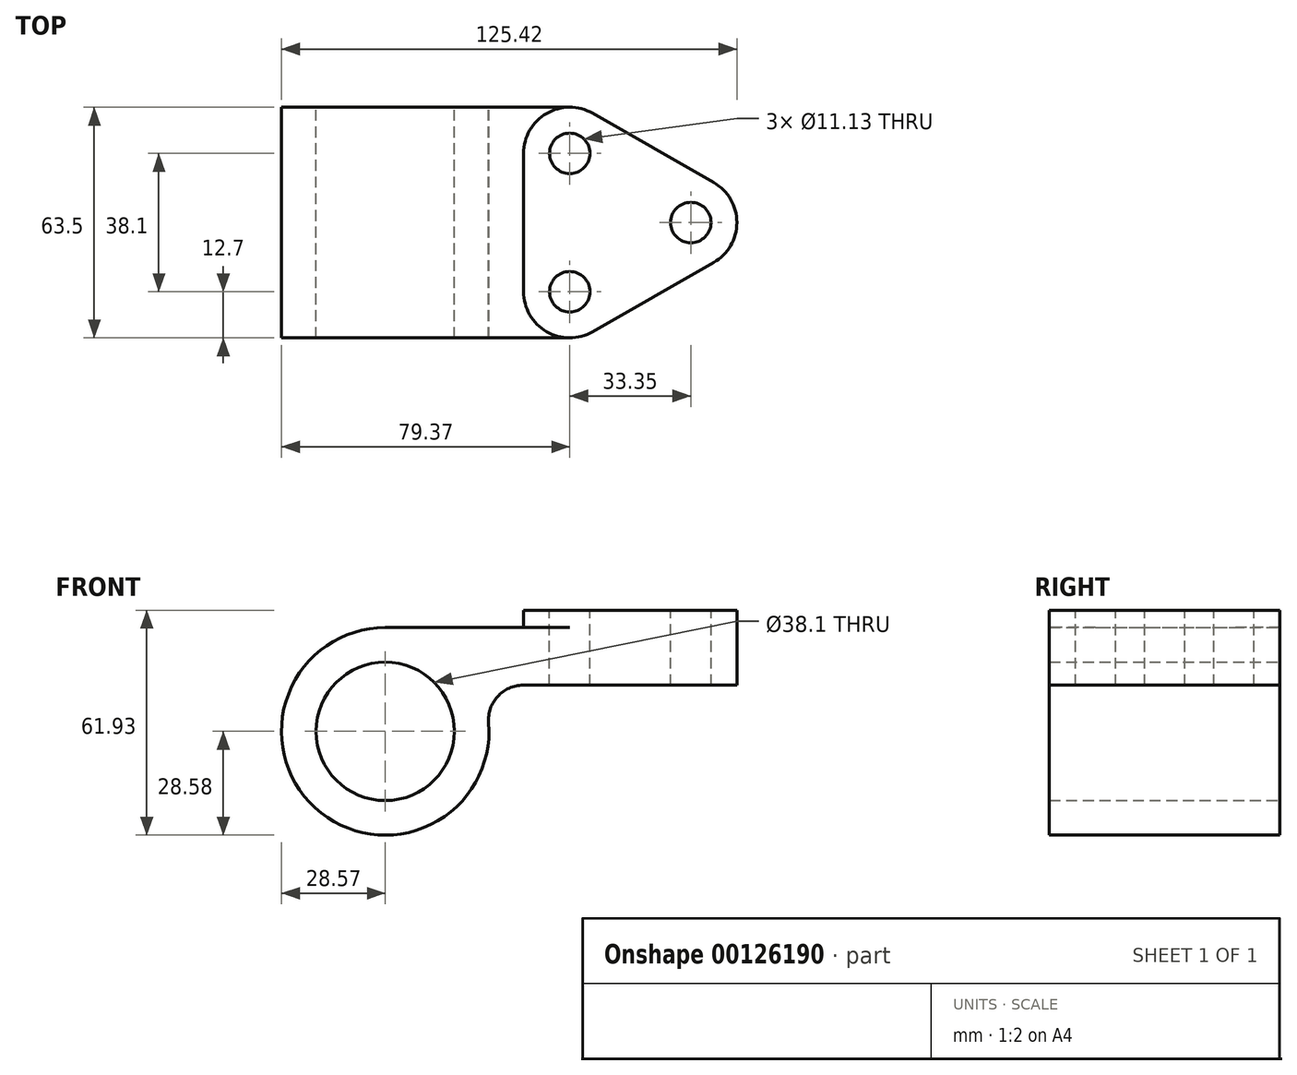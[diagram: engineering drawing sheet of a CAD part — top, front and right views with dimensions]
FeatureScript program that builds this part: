
annotation { "Feature Type Name" : "Feature", "Feature Type Description" : "" }
export const myFeature = defineFeature(function(context is Context, id is Id, definition is map)
    precondition{}
    {
        {
            var Q0;
            Q0=qCreatedBy(makeId("Front.planeOp"),FACE);
            var sketch = newSketch(context, id + "F0", { "sketchPlane" : qUnion([Q0])});
            skArc(sketch, "E0", {"start": v(0, 28.58) * mm, "mid": v(-19.35, -21.03) * mm, "end": v(28.48, 2.38) * mm});
            skArc(sketch, "E1", {"start": v(37.97, 12.7) * mm, "mid": v(30.96, 9.62) * mm, "end": v(28.48, 2.38) * mm});
            skLineSegment(sketch, "E2", {"start": v(0, 28.58) * mm, "end": v(38.1, 28.58) * mm});
            skCircle(sketch, "E3", {"center": v(0, 0) * mm, "radius": 19.05 * mm});
            skLineSegment(sketch, "E4", {"start": v(38.1, 28.58) * mm, "end": v(38.1, 33.35) * mm});
            skLineSegment(sketch, "E5", {"start": v(38.1, 33.35) * mm, "end": v(96.85, 33.35) * mm});
            skLineSegment(sketch, "E6", {"start": v(96.85, 33.35) * mm, "end": v(96.85, 12.7) * mm});
            skLineSegment(sketch, "E7", {"start": v(37.97, 12.7) * mm, "end": v(96.85, 12.7) * mm});
            skLineSegment(sketch, "E8", {"start": v(19.74, -20.66) * mm, "end": v(69.85, 12.7) * mm, "construction": true});
            skLineSegment(sketch, "E9", {"start": v(84.15, 12.7) * mm, "end": v(84.15, 33.35) * mm, "construction": true});
            skLineSegment(sketch, "E10", {"start": v(50.8, 12.7) * mm, "end": v(50.8, 33.35) * mm, "construction": true});
            skSolve(sketch);
        }
        {
            var Q0;
            Q0 = qSketchRegion(id + "F0", true);
            extrude(context, id + "F1", {"entities" : qUnion([Q0]), "depth" : 63.5 * mm});
        }
        {
            var Q0;
            Q0=makeQuery(id+"F1.opExtrude","SWEPT_FACE",FACE,{"disambiguationData":[OSD([sQuery(id+"F0.wireOp",EDGE,"E5")])]});
            var sketch = newSketch(context, id + "F2", { "sketchPlane" : qUnion([Q0])});
            skCircle(sketch, "E11", {"center": v(50.8, -12.7) * mm, "radius": 5.56 * mm});
            skCircle(sketch, "E12", {"center": v(50.8, -50.8) * mm, "radius": 5.56 * mm});
            skCircle(sketch, "E13", {"center": v(84.15, -31.75) * mm, "radius": 5.56 * mm});
            skLineSegment(sketch, "E14", {"start": v(96.85, -31.75) * mm, "end": v(-50.82, -31.75) * mm, "construction": true});
            skPoint(sketch, "E14.endSnap0", {"position": v(96.85, -31.75) * mm});
            skLineSegment(sketch, "E15", {"start": v(84.15, -87.19) * mm, "end": v(84.15, 6.07) * mm, "construction": true});
            skLineSegment(sketch, "E16", {"start": v(33.35, -98.65) * mm, "end": v(33.35, 81.53) * mm, "construction": true});
            skLineSegment(sketch, "E17", {"start": v(50.8, 11.94) * mm, "end": v(50.8, -91.8) * mm, "construction": true});
            skArc(sketch, "E18", {"start": v(90.45, -42.78) * mm, "mid": v(96.85, -31.75) * mm, "end": v(90.45, -20.72) * mm});
            skArc(sketch, "E19", {"start": v(57.1, -1.67) * mm, "mid": v(44.42, -1.72) * mm, "end": v(38.1, -12.7) * mm});
            skArc(sketch, "E20", {"start": v(38.1, -50.8) * mm, "mid": v(44.42, -61.78) * mm, "end": v(57.1, -61.83) * mm});
            skLineSegment(sketch, "E21", {"start": v(57.1, -1.67) * mm, "end": v(90.45, -20.72) * mm});
            skLineSegment(sketch, "E22", {"start": v(90.45, -42.78) * mm, "end": v(57.1, -61.83) * mm});
            skLineSegment(sketch, "E23", {"start": v(38.1, -50.8) * mm, "end": v(38.1, -12.7) * mm});
            skSolve(sketch);
        }
        {
            var Q0;
            Q0=makeQuery(id+"F2.imprint","IMPRINT",FACE,{"disambiguationData":[TD([[makeQuery(id+"F2.imprint","IMPRINT",EDGE,{"derivedFrom":sQuery(id+"F2.wireOp",EDGE,"E12")}),1.0]])]});
            var Q1;
            Q1=makeQuery(id+"F2.imprint","IMPRINT",FACE,{"disambiguationData":[TD([[makeQuery(id+"F2.imprint","IMPRINT",EDGE,{"derivedFrom":sQuery(id+"F2.wireOp",EDGE,"E11")}),1.0]])]});
            var Q2;
            Q2=makeQuery(id+"F2.imprint","IMPRINT",FACE,{"disambiguationData":[TD([[makeQuery(id+"F2.imprint","IMPRINT",EDGE,{"derivedFrom":sQuery(id+"F2.wireOp",EDGE,"E13")}),1.0]])]});
            extrude(context, id + "F3", {"entities" : qUnion([Q0, Q1, Q2]), "operationType" : NewBodyOperationType.REMOVE, "endBound" : BoundingType.THROUGH_ALL, "oppositeDirection" : true, "depth" : 25.4 * mm});
        }
        {
            var Q0;
            {var subQ0=sQuery(id+"F2.wireOp",EDGE,"E19");var subQ1=sQuery(id+"F0.wireOp",EDGE,"E5");var subQ4=makeQuery(id+"F1.opExtrude","CAP_EDGE",EDGE,{"disambiguationData":[OSD([subQ1])],"isStart":true});var subQ5=makeQuery(id+"F2.imprint","INTERSECT",VERTEX,{"derivedFrom":[subQ4,subQ0]});Q0=makeQuery(id+"F2.imprint","IMPRINT",FACE,{"disambiguationData":[TD([[makeQuery(id+"F2.imprint","IMPRINT",EDGE,{"disambiguationData":[TD([[subQ5,1.0]])],"derivedFrom":subQ4}),-1.0]])]});}
            var Q1;
            {var subQ0=sQuery(id+"F2.wireOp",EDGE,"E20");var subQ1=sQuery(id+"F0.wireOp",EDGE,"E5");var subQ4=makeQuery(id+"F1.opExtrude","CAP_EDGE",EDGE,{"disambiguationData":[OSD([subQ1])],"isStart":false});var subQ5=makeQuery(id+"F2.imprint","INTERSECT",VERTEX,{"derivedFrom":[subQ4,subQ0]});Q1=makeQuery(id+"F2.imprint","IMPRINT",FACE,{"disambiguationData":[TD([[makeQuery(id+"F2.imprint","IMPRINT",EDGE,{"disambiguationData":[TD([[subQ5,1.0]])],"derivedFrom":subQ4}),1.0]])]});}
            extrude(context, id + "F4", {"entities" : qUnion([Q0, Q1]), "operationType" : NewBodyOperationType.REMOVE, "oppositeDirection" : true, "depth" : 4.78 * mm});
        }
        {
            var Q0;
            {var subQ6=sQuery(id+"F2.wireOp",EDGE,"E22");Q0=makeQuery(id+"F2.imprint","IMPRINT",FACE,{"disambiguationData":[TD([[makeQuery(id+"F2.imprint","IMPRINT",EDGE,{"derivedFrom":subQ6}),1.0]])]});}
            var Q1;
            {var subQ0=sQuery(id+"F2.wireOp",EDGE,"E21");Q1=makeQuery(id+"F2.imprint","IMPRINT",FACE,{"disambiguationData":[TD([[makeQuery(id+"F2.imprint","IMPRINT",EDGE,{"derivedFrom":subQ0}),1.0]])]});}
            extrude(context, id + "F5", {"entities" : qUnion([Q0, Q1]), "operationType" : NewBodyOperationType.REMOVE, "endBound" : BoundingType.THROUGH_ALL, "oppositeDirection" : true, "depth" : 25.4 * mm});
        }
    });
